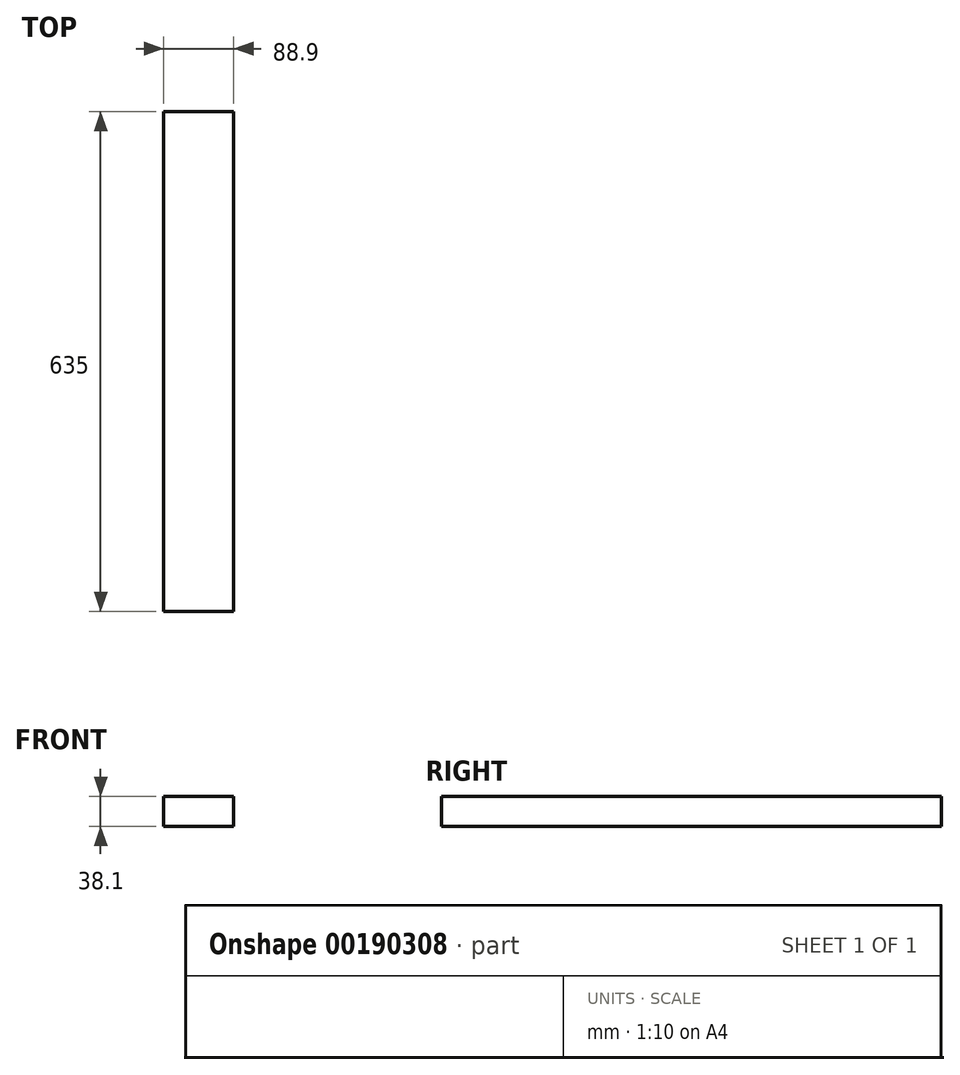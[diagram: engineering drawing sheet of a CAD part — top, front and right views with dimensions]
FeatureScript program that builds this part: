
annotation { "Feature Type Name" : "Feature", "Feature Type Description" : "" }
export const myFeature = defineFeature(function(context is Context, id is Id, definition is map)
    precondition{}
    {
        {
            var Q0;
            Q0=qCreatedBy(makeId("Front.planeOp"),FACE);
            var sketch = newSketch(context, id + "F0", { "sketchPlane" : qUnion([Q0])});
            skLineSegment(sketch, "E0.bottom", {"start": v(44.45, -19.05) * mm, "end": v(-44.45, -19.05) * mm});
            skLineSegment(sketch, "E0.top", {"start": v(44.45, 19.05) * mm, "end": v(-44.45, 19.05) * mm});
            skLineSegment(sketch, "E0.left", {"start": v(44.45, -19.05) * mm, "end": v(44.45, 19.05) * mm});
            skLineSegment(sketch, "E0.right", {"start": v(-44.45, -19.05) * mm, "end": v(-44.45, 19.05) * mm});
            skPoint(sketch, "E0.middle", {"position": v(0, 0) * mm});
            skSolve(sketch);
        }
        {
            var Q0;
            Q0=makeQuery(id+"F0.imprint","IMPRINT",FACE,{"disambiguationData":[TD([[makeQuery(id+"F0.imprint","IMPRINT",EDGE,{"derivedFrom":sQuery(id+"F0.wireOp",EDGE,"E0.bottom")}),-1.0]])]});
            extrude(context, id + "F1", {"entities" : qUnion([Q0]), "depth" : 635 * mm});
        }
    });
